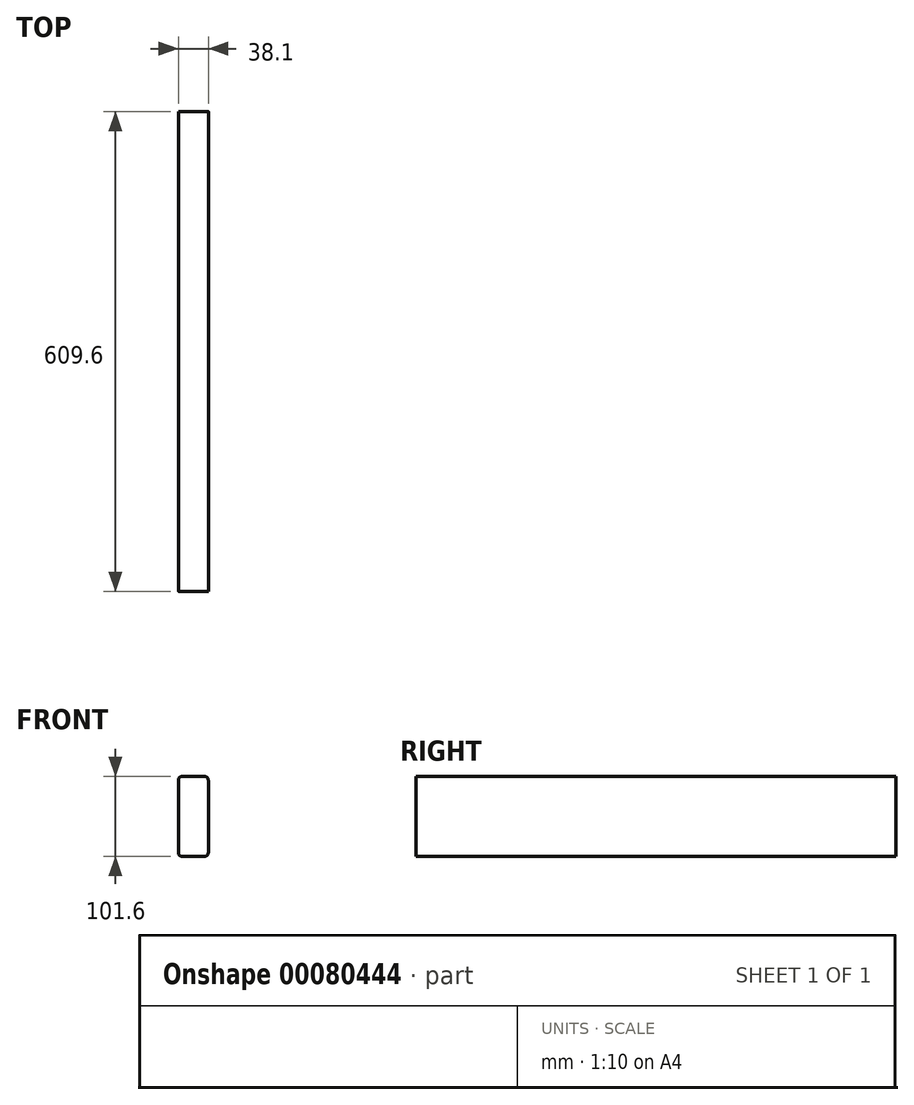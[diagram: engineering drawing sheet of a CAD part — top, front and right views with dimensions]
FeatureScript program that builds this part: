
annotation { "Feature Type Name" : "Feature", "Feature Type Description" : "" }
export const myFeature = defineFeature(function(context is Context, id is Id, definition is map)
    precondition{}
    {
        {
            var Q0;
            Q0=qCreatedBy(makeId("Front.planeOp"),FACE);
            var sketch = newSketch(context, id + "F0", { "sketchPlane" : qUnion([Q0])});
            skLineSegment(sketch, "E0.bottom", {"start": v(-27.1, 54.24) * mm, "end": v(1.47, 54.24) * mm});
            skLineSegment(sketch, "E0.top", {"start": v(-27.1, -47.36) * mm, "end": v(1.47, -47.36) * mm});
            skLineSegment(sketch, "E0.left", {"start": v(-31.86, 49.48) * mm, "end": v(-31.86, -42.6) * mm});
            skLineSegment(sketch, "E0.right", {"start": v(6.24, 49.48) * mm, "end": v(6.24, -42.6) * mm});
            skPoint(sketch, "E1.visualSharp", {"position": v(-31.86, 54.24) * mm});
            skArc(sketch, "E1.filletArc", {"start": v(-27.1, 54.24) * mm, "mid": v(-30.47, 52.84) * mm, "end": v(-31.86, 49.48) * mm});
            skPoint(sketch, "E2.visualSharp", {"position": v(6.24, 54.24) * mm});
            skArc(sketch, "E2.filletArc", {"start": v(6.24, 49.48) * mm, "mid": v(4.84, 52.84) * mm, "end": v(1.47, 54.24) * mm});
            skPoint(sketch, "E3.visualSharp", {"position": v(6.24, -47.36) * mm});
            skArc(sketch, "E3.filletArc", {"start": v(1.47, -47.36) * mm, "mid": v(4.84, -45.97) * mm, "end": v(6.24, -42.6) * mm});
            skPoint(sketch, "E4.visualSharp", {"position": v(-31.86, -47.36) * mm});
            skArc(sketch, "E4.filletArc", {"start": v(-31.86, -42.6) * mm, "mid": v(-30.47, -45.97) * mm, "end": v(-27.1, -47.36) * mm});
            skSolve(sketch);
        }
        {
            var Q0;
            Q0=makeQuery(id+"F0.imprint","IMPRINT",FACE,{"disambiguationData":[TD([[makeQuery(id+"F0.imprint","IMPRINT",EDGE,{"derivedFrom":sQuery(id+"F0.wireOp",EDGE,"E0.bottom")}),-1.0]])]});
            extrude(context, id + "F1", {"entities" : qUnion([Q0]), "depth" : 609.6 * mm});
        }
    });
